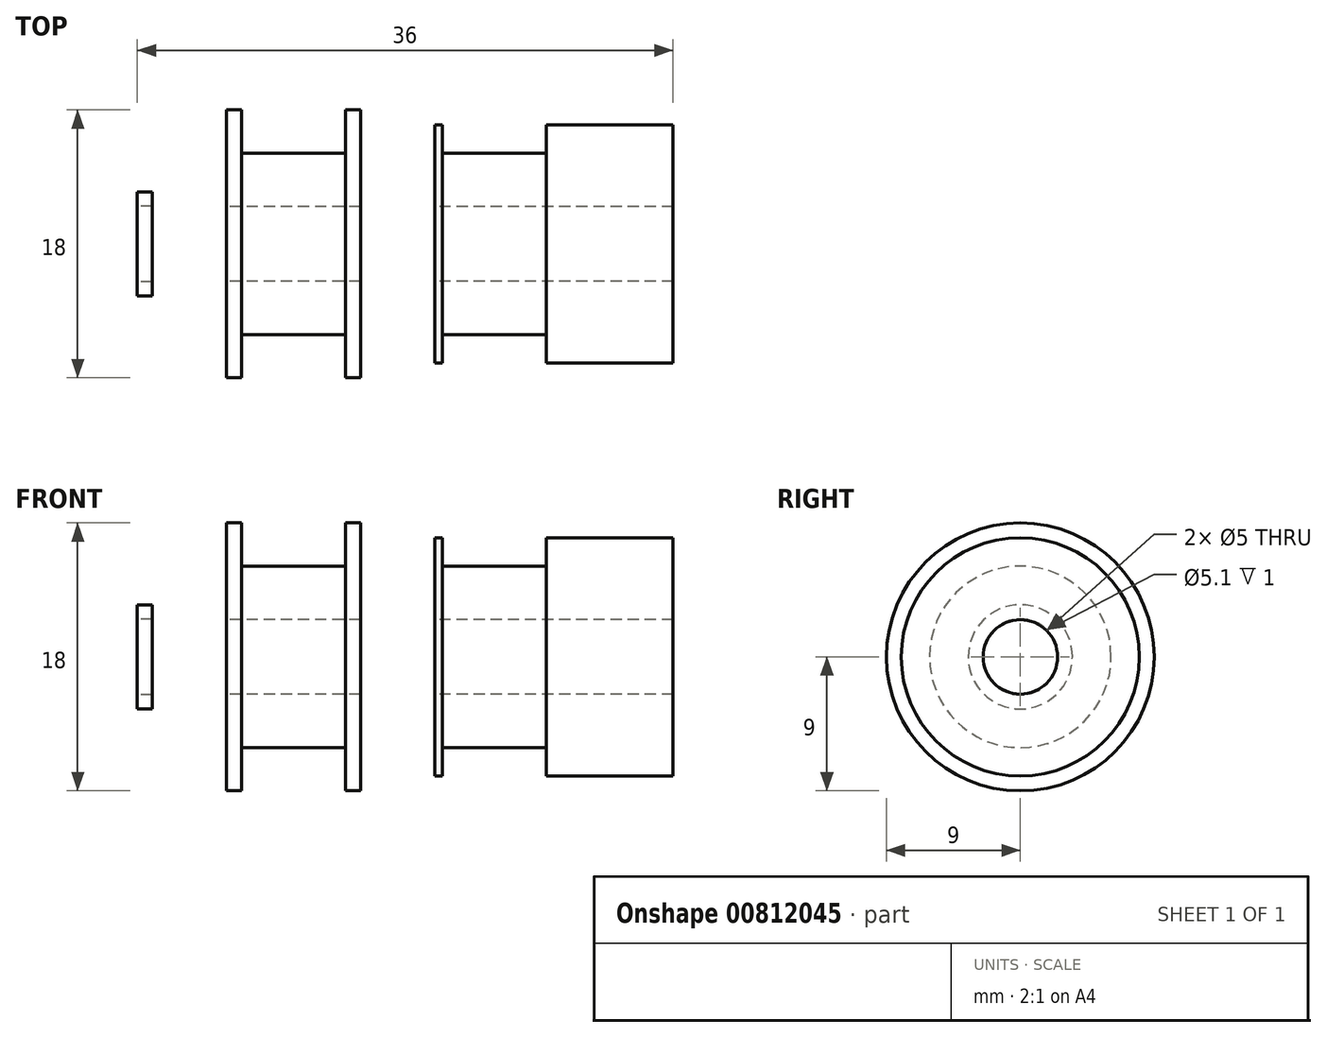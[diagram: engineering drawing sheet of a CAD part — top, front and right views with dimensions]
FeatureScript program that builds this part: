
annotation { "Feature Type Name" : "Feature", "Feature Type Description" : "" }
export const myFeature = defineFeature(function(context is Context, id is Id, definition is map)
    precondition{}
    {
        {
            var Q0;
            Q0=qCreatedBy(makeId("Front.planeOp"),FACE);
            var sketch = newSketch(context, id + "F0", { "sketchPlane" : qUnion([Q0])});
            skLineSegment(sketch, "E0", {"start": v(0, 2.5) * mm, "end": v(0, 8) * mm});
            skLineSegment(sketch, "E1", {"start": v(0, 8) * mm, "end": v(0.5, 8) * mm});
            skLineSegment(sketch, "E2", {"start": v(0.5, 8) * mm, "end": v(0.5, 6.1) * mm});
            skLineSegment(sketch, "E3", {"start": v(0.5, 6.1) * mm, "end": v(7.5, 6.1) * mm});
            skLineSegment(sketch, "E4", {"start": v(7.5, 6.1) * mm, "end": v(7.5, 8) * mm});
            skLineSegment(sketch, "E5", {"start": v(7.5, 8) * mm, "end": v(16, 8) * mm});
            skLineSegment(sketch, "E6", {"start": v(16, 8) * mm, "end": v(16, 2.5) * mm});
            skLineSegment(sketch, "E7", {"start": v(16, 2.5) * mm, "end": v(0, 2.5) * mm});
            skLineSegment(sketch, "E8", {"start": v(0, 0) * mm, "end": v(16, 0) * mm});
            skLineSegment(sketch, "E9", {"start": v(-14, 9) * mm, "end": v(-14, 2.5) * mm});
            skLineSegment(sketch, "E10", {"start": v(-14, 2.5) * mm, "end": v(-5, 2.5) * mm});
            skLineSegment(sketch, "E11", {"start": v(-5, 2.5) * mm, "end": v(-5, 9) * mm});
            skLineSegment(sketch, "E12", {"start": v(-5, 9) * mm, "end": v(-6, 9) * mm});
            skLineSegment(sketch, "E13", {"start": v(-6, 9) * mm, "end": v(-6, 6.1) * mm});
            skLineSegment(sketch, "E14", {"start": v(-6, 6.1) * mm, "end": v(-13, 6.1) * mm});
            skLineSegment(sketch, "E15", {"start": v(-13, 6.1) * mm, "end": v(-13, 9) * mm});
            skLineSegment(sketch, "E16", {"start": v(-13, 9) * mm, "end": v(-14, 9) * mm});
            skLineSegment(sketch, "E17.bottom", {"start": v(-20, 2.55) * mm, "end": v(-19, 2.55) * mm});
            skLineSegment(sketch, "E17.top", {"start": v(-20, 3.5) * mm, "end": v(-19, 3.5) * mm});
            skLineSegment(sketch, "E17.left", {"start": v(-20, 2.55) * mm, "end": v(-20, 3.5) * mm});
            skLineSegment(sketch, "E17.right", {"start": v(-19, 2.55) * mm, "end": v(-19, 3.5) * mm});
            skSolve(sketch);
        }
        {
            var Q0;
            Q0=makeQuery(id+"F0.imprint","IMPRINT",FACE,{"disambiguationData":[TD([[makeQuery(id+"F0.imprint","IMPRINT",EDGE,{"derivedFrom":sQuery(id+"F0.wireOp",EDGE,"E0")}),-1.0]])]});
            var Q1;
            Q1=sQuery(id+"F0.wireOp",EDGE,"E8");
            revolve(context, id + "F1", {"surfaceOperationType" : NewSurfaceOperationType.NEW, "entities" : qUnion([Q0]), "axis" : qUnion([Q1]), "revolveType" : RevolveType.FULL});
        }
        {
            var Q0;
            Q0=makeQuery(id+"F0.imprint","IMPRINT",FACE,{"disambiguationData":[TD([[makeQuery(id+"F0.imprint","IMPRINT",EDGE,{"derivedFrom":sQuery(id+"F0.wireOp",EDGE,"E9")}),1.0]])]});
            var Q1;
            Q1=sQuery(id+"F0.wireOp",EDGE,"E8");
            revolve(context, id + "F2", {"surfaceOperationType" : NewSurfaceOperationType.NEW, "entities" : qUnion([Q0]), "axis" : qUnion([Q1]), "revolveType" : RevolveType.FULL});
        }
        {
            var Q0;
            Q0=makeQuery(id+"F0.imprint","IMPRINT",FACE,{"disambiguationData":[TD([[makeQuery(id+"F0.imprint","IMPRINT",EDGE,{"derivedFrom":sQuery(id+"F0.wireOp",EDGE,"E17.bottom")}),1.0]])]});
            var Q1;
            Q1=sQuery(id+"F0.wireOp",EDGE,"E8");
            revolve(context, id + "F3", {"surfaceOperationType" : NewSurfaceOperationType.NEW, "entities" : qUnion([Q0]), "axis" : qUnion([Q1]), "revolveType" : RevolveType.FULL});
        }
    });
